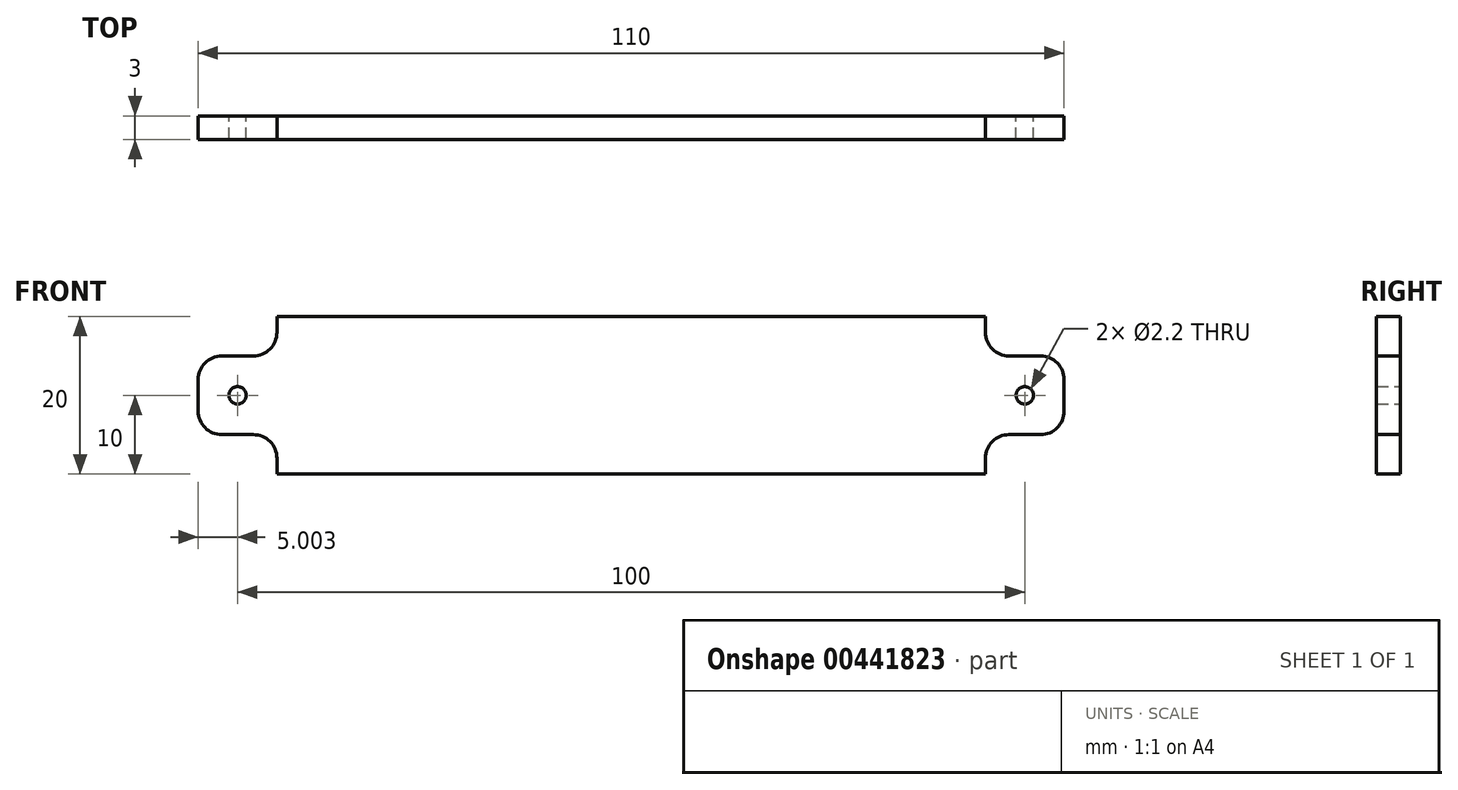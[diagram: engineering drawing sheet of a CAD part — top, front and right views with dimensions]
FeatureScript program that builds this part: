
annotation { "Feature Type Name" : "Feature", "Feature Type Description" : "" }
export const myFeature = defineFeature(function(context is Context, id is Id, definition is map)
    precondition{}
    {
        {
            var Q0;
            Q0=qCreatedBy(makeId("Front.planeOp"),FACE);
            var sketch = newSketch(context, id + "F0", { "sketchPlane" : qUnion([Q0])});
            skLineSegment(sketch, "E0.bottom", {"start": v(-53.14, 20) * mm, "end": v(36.86, 20) * mm});
            skLineSegment(sketch, "E0.top", {"start": v(-53.14, 0) * mm, "end": v(36.86, 0) * mm});
            skLineSegment(sketch, "E0.left", {"start": v(-53.14, 20) * mm, "end": v(-53.14, 15) * mm});
            skLineSegment(sketch, "E0.right", {"start": v(36.86, 20) * mm, "end": v(36.86, 18) * mm});
            skLineSegment(sketch, "E1.bottom", {"start": v(-53.14, 15) * mm, "end": v(-63.14, 15) * mm});
            skLineSegment(sketch, "E1.top", {"start": v(-53.14, 5) * mm, "end": v(-63.14, 5) * mm});
            skLineSegment(sketch, "E1.right", {"start": v(-63.14, 15) * mm, "end": v(-63.14, 5) * mm});
            skLineSegment(sketch, "E2", {"start": v(-8.14, 20) * mm, "end": v(-8.14, 11.54) * mm, "construction": true});
            skLineSegment(sketch, "E3.MirrorCS", {"start": v(39.86, 15) * mm, "end": v(46.86, 15) * mm});
            skLineSegment(sketch, "E4.MirrorCS", {"start": v(46.86, 15) * mm, "end": v(46.86, 5) * mm});
            skLineSegment(sketch, "E5.MirrorCS", {"start": v(39.86, 5) * mm, "end": v(46.86, 5) * mm});
            skLineSegment(sketch, "E6.trimOffspring", {"start": v(36.86, 2) * mm, "end": v(36.86, 0) * mm});
            skLineSegment(sketch, "E7.trimOffspring", {"start": v(-53.14, 5) * mm, "end": v(-53.14, 0) * mm});
            skPoint(sketch, "E8.visualSharp", {"position": v(46.86, 15) * mm});
            skPoint(sketch, "E9.visualSharp", {"position": v(36.86, 15) * mm});
            skArc(sketch, "E9.filletArc", {"start": v(36.86, 18) * mm, "mid": v(37.74, 15.88) * mm, "end": v(39.86, 15) * mm});
            skPoint(sketch, "E10.visualSharp", {"position": v(36.86, 5) * mm});
            skArc(sketch, "E10.filletArc", {"start": v(39.86, 5) * mm, "mid": v(37.74, 4.12) * mm, "end": v(36.86, 2) * mm});
            skCircle(sketch, "E11", {"center": v(-58.14, 10) * mm, "radius": 1.1 * mm});
            skPoint(sketch, "E11.centerSnap0", {"position": v(-63.14, 10) * mm});
            skPoint(sketch, "E11.centerSnap1", {"position": v(-58.14, 15) * mm});
            skCircle(sketch, "E12.MirrorC", {"center": v(41.86, 10) * mm, "radius": 1.1 * mm});
            skSolve(sketch);
        }
        {
            var Q0;
            Q0 = qSketchRegion(id + "F0", true);
            extrude(context, id + "F1", {"entities" : qUnion([Q0]), "depth" : 3 * mm});
        }
        {
            var Q0;
            Q0=makeQuery(id+"F1.opExtrude","SWEPT_EDGE",EDGE,{"disambiguationData":[OSD([sQuery(id+"F0.wireOp",EDGE,"E0.left"),sQuery(id+"F0.wireOp",EDGE,"E1.bottom")])]});
            var Q1;
            Q1=makeQuery(id+"F1.opExtrude","SWEPT_EDGE",EDGE,{"disambiguationData":[OSD([sQuery(id+"F0.wireOp",EDGE,"E1.top"),sQuery(id+"F0.wireOp",EDGE,"E7.trimOffspring")])]});
            var Q2;
            Q2=makeQuery(id+"F1.opExtrude","SWEPT_EDGE",EDGE,{"disambiguationData":[OSD([sQuery(id+"F0.wireOp",EDGE,"E1.bottom"),sQuery(id+"F0.wireOp",EDGE,"E1.right")])]});
            var Q3;
            Q3=makeQuery(id+"F1.opExtrude","SWEPT_EDGE",EDGE,{"disambiguationData":[OSD([sQuery(id+"F0.wireOp",EDGE,"E1.top"),sQuery(id+"F0.wireOp",EDGE,"E1.right")])]});
            var Q4;
            Q4=makeQuery(id+"F1.opExtrude","SWEPT_EDGE",EDGE,{"disambiguationData":[OSD([sQuery(id+"F0.wireOp",EDGE,"E4.MirrorCS"),sQuery(id+"F0.wireOp",EDGE,"E5.MirrorCS")])]});
            var Q5;
            Q5=makeQuery(id+"F1.opExtrude","SWEPT_EDGE",EDGE,{"disambiguationData":[OSD([sQuery(id+"F0.wireOp",EDGE,"E3.MirrorCS"),sQuery(id+"F0.wireOp",EDGE,"E4.MirrorCS")])]});
            fillet(context, id + "F2", {"entities" : qUnion([Q0, Q1, Q2, Q3, Q4, Q5]), "radius" : 3 * mm, "tangentPropagation" : true, "allowEdgeOverflow" : false});
        }
    });
